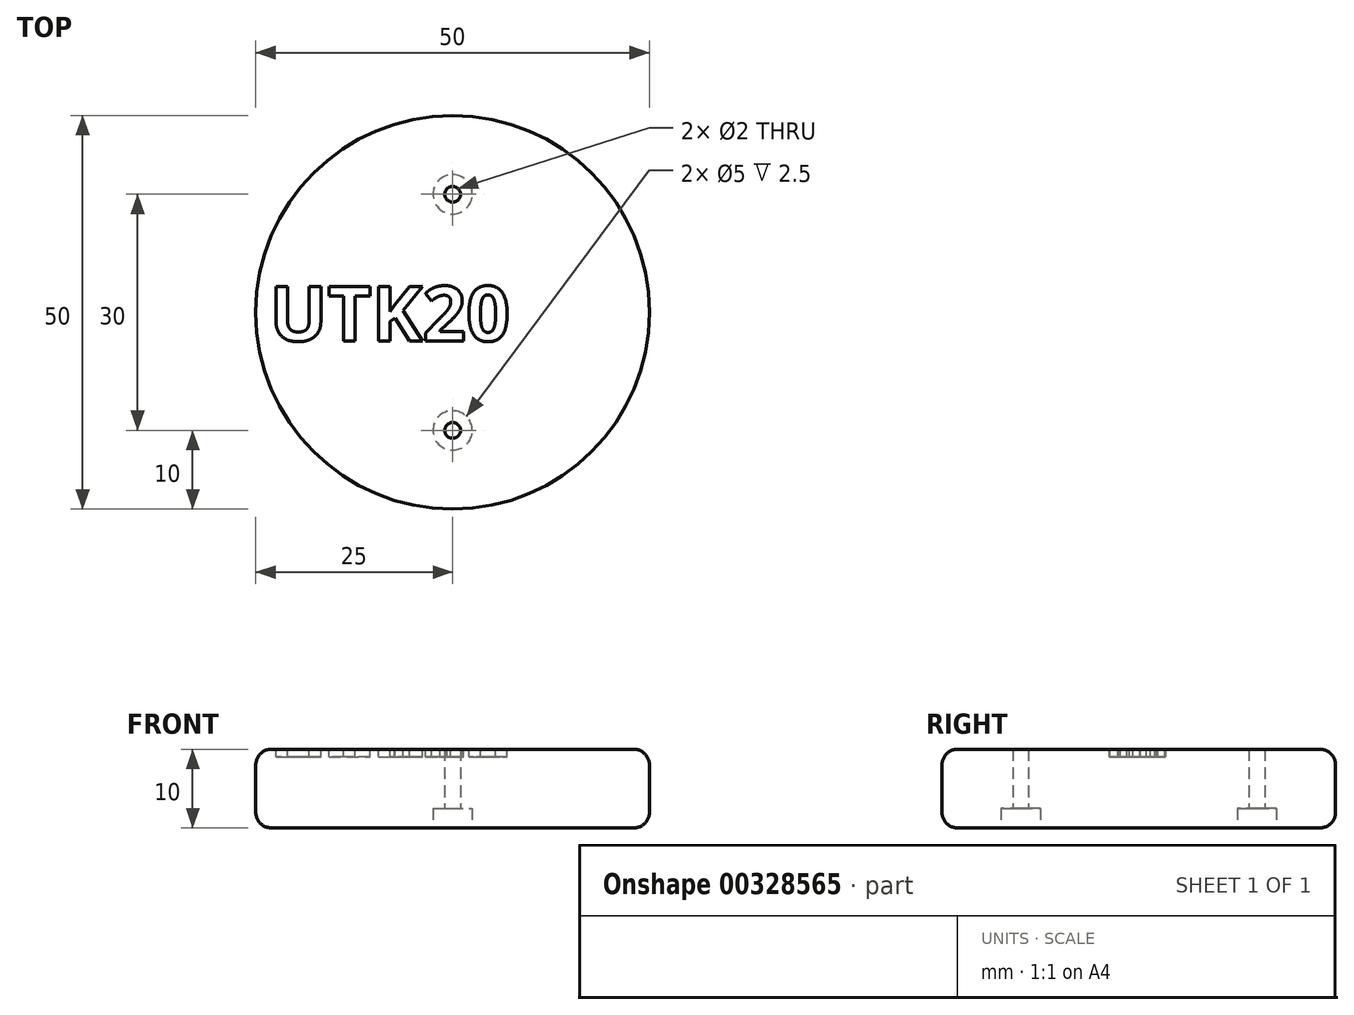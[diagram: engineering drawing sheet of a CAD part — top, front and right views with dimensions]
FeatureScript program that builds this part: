
annotation { "Feature Type Name" : "Feature", "Feature Type Description" : "" }
export const myFeature = defineFeature(function(context is Context, id is Id, definition is map)
    precondition{}
    {
        {
            var Q0;
            Q0=qCreatedBy(makeId("Top.planeOp"),FACE);
            var sketch = newSketch(context, id + "F0", { "sketchPlane" : qUnion([Q0])});
            skCircle(sketch, "E0", {"center": v(0, 0) * mm, "radius": 25 * mm});
            skSolve(sketch);
        }
        {
            var Q0;
            Q0=qSketchRegion(id+"F0",true);
            extrude(context, id + "F1", {"entities" : qUnion([Q0]), "depth" : 10 * mm});
        }
        {
            var Q0;
            Q0=makeQuery(id+"F1.opExtrude","CAP_FACE",FACE,{"disambiguationData":[OSD([sQuery(id+"F0.wireOp",EDGE,"E0")])],"isStart":false});
            var sketch = newSketch(context, id + "F2", { "sketchPlane" : qUnion([Q0])});
            skText(sketch, "E1", { "text": "UTK20", "fontName": "OpenSans-Bold.ttf"});
            const initialGuessF2  = {"E1": [-0.02326, -0.00364, 1, 0, 0.007]};
            skSetInitialGuess(sketch, initialGuessF2);
            skSolve(sketch);
        }
        {
            var Q0;
            Q0=qSketchRegion(id+"F2",true);
            extrude(context, id + "F3", {"entities" : qUnion([Q0]), "operationType" : NewBodyOperationType.REMOVE, "oppositeDirection" : true, "depth" : 1 * mm});
        }
        {
            var Q0;
            Q0=makeQuery(id+"F1.opExtrude","CAP_EDGE",EDGE,{"disambiguationData":[OSD([sQuery(id+"F0.wireOp",EDGE,"E0")])],"isStart":false});
            var Q1;
            Q1=makeQuery(id+"F1.opExtrude","CAP_EDGE",EDGE,{"disambiguationData":[OSD([sQuery(id+"F0.wireOp",EDGE,"E0")])],"isStart":true});
            fillet(context, id + "F4", {"entities" : qUnion([Q0, Q1]), "radius" : 2 * mm, "tangentPropagation" : true, "allowEdgeOverflow" : false});
        }
        {
            var Q0;
            Q0=makeQuery(id+"F1.opExtrude","CAP_FACE",FACE,{"disambiguationData":[OSD([sQuery(id+"F0.wireOp",EDGE,"E0")])],"isStart":true});
            var sketch = newSketch(context, id + "F5", { "sketchPlane" : qUnion([Q0])});
            skPoint(sketch, "E2", {"position": v(0, 15) * mm});
            skPoint(sketch, "E3", {"position": v(0, -15) * mm});
            skSolve(sketch);
        }
        {
            var Q0;
            Q0=sQuery(id+"F5.wireOp",VERTEX,"E2");
            var Q1;
            Q1=sQuery(id+"F5.wireOp",VERTEX,"E3");
            var Q2;
            Q2=makeQuery(id+"F1.opExtrude","SWEPT_BODY",BODY,{"disambiguationData":[OSD([sQuery(id+"F0.wireOp",EDGE,"E0")])]});
            hole(context, id + "F6", {"style" : HoleStyle.C_BORE, "endStyle" : HoleEndStyle.THROUGH, "holeDiameter" : 2 * mm, "cBoreDiameter" : 5 * mm, "cBoreDepth" : 2.5 * mm, "startFromSketch" : true, "locations" : qUnion([Q0, Q1]), "scope" : qUnion([Q2]), "isTappedThrough" : true});
        }
    });
